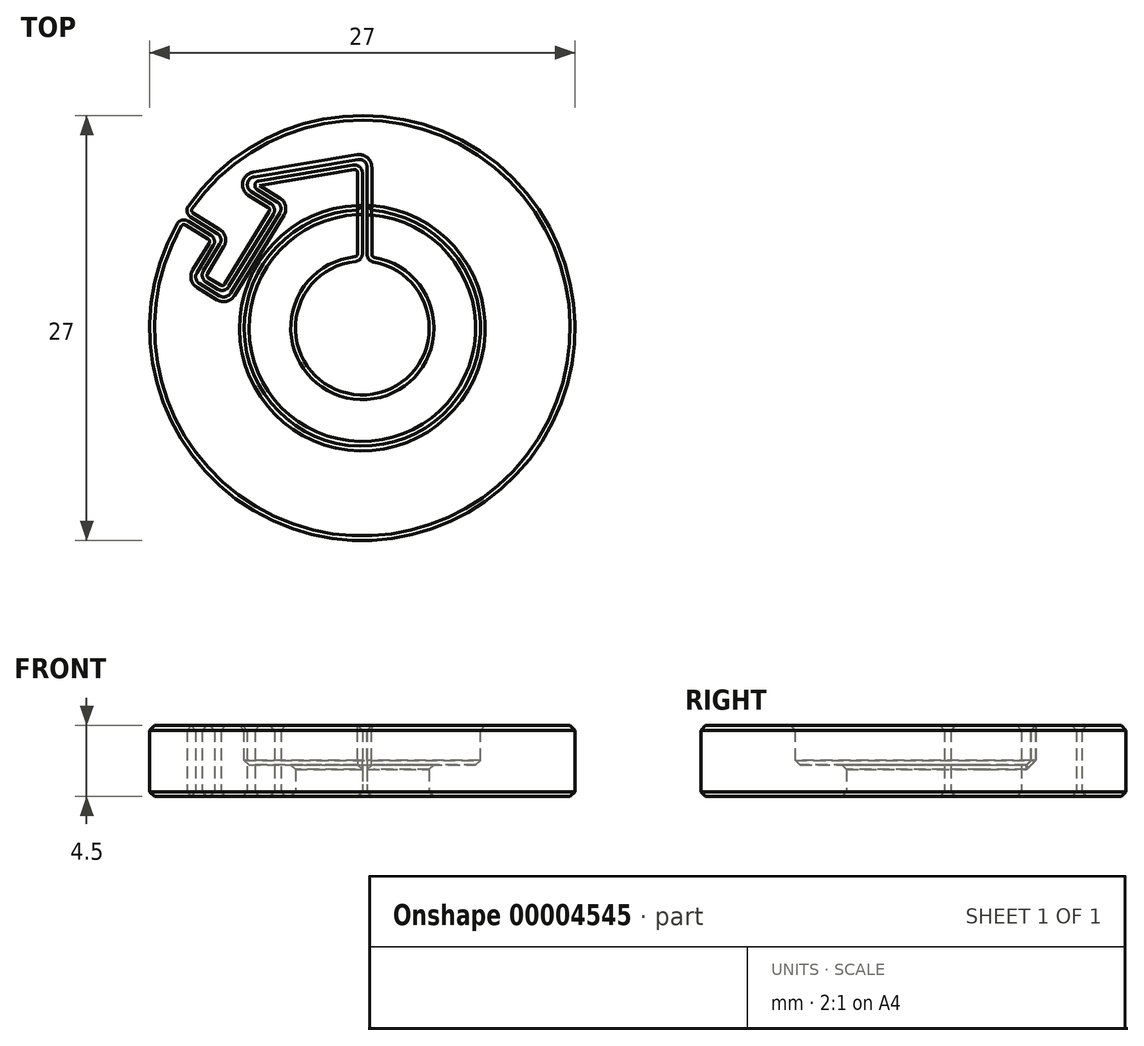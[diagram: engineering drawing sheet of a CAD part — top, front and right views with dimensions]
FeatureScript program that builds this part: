
annotation { "Feature Type Name" : "Feature", "Feature Type Description" : "" }
export const myFeature = defineFeature(function(context is Context, id is Id, definition is map)
    precondition{}
    {
        {
            var Q0;
            Q0=qCreatedBy(makeId("Top.planeOp"),FACE);
            var sketch = newSketch(context, id + "F0", { "sketchPlane" : qUnion([Q0])});
            skArc(sketch, "E0", {"start": v(-0.45, 4.23) * mm, "mid": v(-0.14, -4.25) * mm, "end": v(0.72, 4.19) * mm});
            skArc(sketch, "E1", {"start": v(-11.77, 6.62) * mm, "mid": v(11.42, -7.2) * mm, "end": v(-11.05, 7.76) * mm});
            skLineSegment(sketch, "E2", {"start": v(0, 13.5) * mm, "end": v(0, 4.25) * mm, "construction": true});
            skLineSegment(sketch, "E3", {"start": v(-0.58, 10.35) * mm, "end": v(-6.58, 9.35) * mm});
            skLineSegment(sketch, "E4", {"start": v(-6.69, 8.8) * mm, "end": v(-5.4, 8.01) * mm});
            skLineSegment(sketch, "E5", {"start": v(-9.63, 5.91) * mm, "end": v(-11.07, 6.8) * mm});
            skLineSegment(sketch, "E6", {"start": v(0, 9.86) * mm, "end": v(0, 4.72) * mm});
            skLineSegment(sketch, "E7.0", {"start": v(-9.22, 6.01) * mm, "end": v(-10.9, 7.04) * mm});
            skLineSegment(sketch, "E7.1", {"start": v(0.3, 10.21) * mm, "end": v(0.3, 4.68) * mm});
            skLineSegment(sketch, "E7.2", {"start": v(-0.28, 10.7) * mm, "end": v(-6.9, 9.6) * mm});
            skLineSegment(sketch, "E7.3", {"start": v(-7.07, 8.68) * mm, "end": v(-5.82, 7.91) * mm});
            skPoint(sketch, "E8.visualSharp", {"position": v(0, 10.45) * mm});
            skArc(sketch, "E8.filletArc", {"start": v(0, 9.86) * mm, "mid": v(-0.18, 10.24) * mm, "end": v(-0.58, 10.35) * mm});
            skPoint(sketch, "E9.visualSharp", {"position": v(-7.37, 9.22) * mm});
            skArc(sketch, "E9.filletArc", {"start": v(-6.58, 9.35) * mm, "mid": v(-6.82, 9.11) * mm, "end": v(-6.69, 8.8) * mm});
            skArc(sketch, "E10.filletArc", {"start": v(-5.24, 7.33) * mm, "mid": v(-5.18, 7.7) * mm, "end": v(-5.4, 8.01) * mm});
            skPoint(sketch, "E11.visualSharp", {"position": v(-6.4, 3.92) * mm});
            skPoint(sketch, "E12.visualSharp", {"position": v(-6.45, 4.31) * mm});
            skPoint(sketch, "E13.visualSharp", {"position": v(-4.54, 7.13) * mm});
            skArc(sketch, "E13.filletArc", {"start": v(-5.65, 7.23) * mm, "mid": v(-5.6, 7.6) * mm, "end": v(-5.82, 7.91) * mm});
            skPoint(sketch, "E14.visualSharp", {"position": v(0.3, 10.8) * mm});
            skArc(sketch, "E14.filletArc", {"start": v(0.3, 10.21) * mm, "mid": v(0.12, 10.6) * mm, "end": v(-0.28, 10.7) * mm});
            skPoint(sketch, "E15.visualSharp", {"position": v(-8.2, 9.38) * mm});
            skArc(sketch, "E15.filletArc", {"start": v(-6.9, 9.6) * mm, "mid": v(-7.3, 9.2) * mm, "end": v(-7.07, 8.68) * mm});
            skLineSegment(sketch, "E16", {"start": v(-9.47, 5.22) * mm, "end": v(-10.51, 3.52) * mm});
            skLineSegment(sketch, "E17", {"start": v(-10.35, 2.83) * mm, "end": v(-9.07, 2.05) * mm});
            skLineSegment(sketch, "E18", {"start": v(-8.38, 2.21) * mm, "end": v(-5.24, 7.33) * mm});
            skLineSegment(sketch, "E19.0", {"start": v(-8.48, 2.62) * mm, "end": v(-5.65, 7.23) * mm});
            skLineSegment(sketch, "E19.1", {"start": v(-9.93, 2.93) * mm, "end": v(-9.17, 2.46) * mm});
            skLineSegment(sketch, "E19.2", {"start": v(-9.05, 5.32) * mm, "end": v(-10.1, 3.62) * mm});
            skPoint(sketch, "E20.visualSharp", {"position": v(-8.64, 1.79) * mm});
            skArc(sketch, "E20.filletArc", {"start": v(-9.07, 2.05) * mm, "mid": v(-8.7, 1.99) * mm, "end": v(-8.38, 2.21) * mm});
            skPoint(sketch, "E21.visualSharp", {"position": v(-10.77, 3.1) * mm});
            skArc(sketch, "E21.filletArc", {"start": v(-10.51, 3.52) * mm, "mid": v(-10.57, 3.14) * mm, "end": v(-10.35, 2.83) * mm});
            skPoint(sketch, "E22.visualSharp", {"position": v(-10.36, 3.2) * mm});
            skArc(sketch, "E22.filletArc", {"start": v(-10.1, 3.62) * mm, "mid": v(-10.16, 3.24) * mm, "end": v(-9.93, 2.93) * mm});
            skPoint(sketch, "E23.visualSharp", {"position": v(-8.74, 2.2) * mm});
            skArc(sketch, "E23.filletArc", {"start": v(-9.17, 2.46) * mm, "mid": v(-8.79, 2.4) * mm, "end": v(-8.48, 2.62) * mm});
            skPoint(sketch, "E24.visualSharp", {"position": v(-9.2, 5.65) * mm});
            skArc(sketch, "E24.filletArc", {"start": v(-9.47, 5.22) * mm, "mid": v(-9.4, 5.6) * mm, "end": v(-9.63, 5.91) * mm});
            skPoint(sketch, "E25.visualSharp", {"position": v(-8.8, 5.75) * mm});
            skArc(sketch, "E25.filletArc", {"start": v(-9.05, 5.32) * mm, "mid": v(-9, 5.7) * mm, "end": v(-9.22, 6.01) * mm});
            skPoint(sketch, "E26.visualSharp", {"position": v(-11.5, 7.06) * mm});
            skArc(sketch, "E26.filletArc", {"start": v(-11.07, 6.8) * mm, "mid": v(-11.46, 6.85) * mm, "end": v(-11.77, 6.62) * mm});
            skPoint(sketch, "E27.visualSharp", {"position": v(-11.35, 7.32) * mm});
            skArc(sketch, "E27.filletArc", {"start": v(-11.05, 7.76) * mm, "mid": v(-11.13, 7.37) * mm, "end": v(-10.9, 7.04) * mm});
            skPoint(sketch, "E28.visualSharp", {"position": v(0, 4.25) * mm});
            skArc(sketch, "E28.filletArc", {"start": v(-0.45, 4.23) * mm, "mid": v(-0.13, 4.39) * mm, "end": v(0, 4.72) * mm});
            skPoint(sketch, "E29.visualSharp", {"position": v(0.3, 4.24) * mm});
            skArc(sketch, "E29.filletArc", {"start": v(0.3, 4.68) * mm, "mid": v(0.42, 4.36) * mm, "end": v(0.72, 4.19) * mm});
            skSolve(sketch);
        }
        {
            var Q0;
            Q0=makeQuery(id+"F0.imprint","IMPRINT",FACE,{"disambiguationData":[TD([[makeQuery(id+"F0.imprint","IMPRINT",EDGE,{"derivedFrom":sQuery(id+"F0.wireOp",EDGE,"E3")}),1.0]])]});
            extrude(context, id + "F1", {"entities" : qUnion([Q0]), "depth" : (2 + 2.5) * mm, "offsetDistance" : 25 * mm});
        }
        {
            var Q0;
            Q0=makeQuery(id+"F1.opExtrude","CAP_FACE",FACE,{"disambiguationData":[OSD([sQuery(id+"F0.wireOp",EDGE,"E0"),sQuery(id+"F0.wireOp",EDGE,"E1"),sQuery(id+"F0.wireOp",EDGE,"E3"),sQuery(id+"F0.wireOp",EDGE,"E4"),sQuery(id+"F0.wireOp",EDGE,"27mV3W1z-r9zT-I5jQ-fDVQ-ZefElLG8ptBj"),sQuery(id+"F0.wireOp",EDGE,"E5"),sQuery(id+"F0.wireOp",EDGE,"E6"),sQuery(id+"F0.wireOp",EDGE,"E7.0"),sQuery(id+"F0.wireOp",EDGE,"E7.1"),sQuery(id+"F0.wireOp",EDGE,"E7.2"),sQuery(id+"F0.wireOp",EDGE,"E7.3"),sQuery(id+"F0.wireOp",EDGE,"E7.4")])],"isStart":false});
            var sketch = newSketch(context, id + "F2", { "sketchPlane" : qUnion([Q0])});
            skCircle(sketch, "E30", {"center": v(0, 0) * mm, "radius": 7.5 * mm});
            skSolve(sketch);
        }
        {
            var Q0;
            Q0 = qSketchRegion(id + "F2", true);
            extrude(context, id + "F3", {"entities" : qUnion([Q0]), "operationType" : NewBodyOperationType.REMOVE, "oppositeDirection" : true, "depth" : 2.5 * mm, "offsetDistance" : 25 * mm});
        }
        {
            var Q0;
            Q0=makeQuery(id+"F1.opExtrude","CAP_FACE",FACE,{"disambiguationData":[OSD([sQuery(id+"F0.wireOp",EDGE,"E0"),sQuery(id+"F0.wireOp",EDGE,"E1"),sQuery(id+"F0.wireOp",EDGE,"E3"),sQuery(id+"F0.wireOp",EDGE,"E4"),sQuery(id+"F0.wireOp",EDGE,"E5"),sQuery(id+"F0.wireOp",EDGE,"E6"),sQuery(id+"F0.wireOp",EDGE,"E7.0"),sQuery(id+"F0.wireOp",EDGE,"E7.1"),sQuery(id+"F0.wireOp",EDGE,"E7.2"),sQuery(id+"F0.wireOp",EDGE,"E7.3"),sQuery(id+"F0.wireOp",EDGE,"E8.filletArc"),sQuery(id+"F0.wireOp",EDGE,"E9.filletArc"),sQuery(id+"F0.wireOp",EDGE,"E10.filletArc"),sQuery(id+"F0.wireOp",EDGE,"E13.filletArc"),sQuery(id+"F0.wireOp",EDGE,"E14.filletArc"),sQuery(id+"F0.wireOp",EDGE,"E15.filletArc"),sQuery(id+"F0.wireOp",EDGE,"E16"),sQuery(id+"F0.wireOp",EDGE,"E17"),sQuery(id+"F0.wireOp",EDGE,"E18"),sQuery(id+"F0.wireOp",EDGE,"E19.0"),sQuery(id+"F0.wireOp",EDGE,"E19.1"),sQuery(id+"F0.wireOp",EDGE,"E19.2"),sQuery(id+"F0.wireOp",EDGE,"E20.filletArc"),sQuery(id+"F0.wireOp",EDGE,"E21.filletArc"),sQuery(id+"F0.wireOp",EDGE,"E22.filletArc"),sQuery(id+"F0.wireOp",EDGE,"E23.filletArc"),sQuery(id+"F0.wireOp",EDGE,"E24.filletArc"),sQuery(id+"F0.wireOp",EDGE,"E25.filletArc"),sQuery(id+"F0.wireOp",EDGE,"E26.filletArc"),sQuery(id+"F0.wireOp",EDGE,"E27.filletArc"),sQuery(id+"F0.wireOp",EDGE,"E28.filletArc"),sQuery(id+"F0.wireOp",EDGE,"E29.filletArc")])],"isStart":true});
            var Q1;
            Q1=makeQuery(id+"F1.opExtrude","CAP_FACE",FACE,{"disambiguationData":[OSD([sQuery(id+"F0.wireOp",EDGE,"E0"),sQuery(id+"F0.wireOp",EDGE,"E1"),sQuery(id+"F0.wireOp",EDGE,"E3"),sQuery(id+"F0.wireOp",EDGE,"E4"),sQuery(id+"F0.wireOp",EDGE,"E5"),sQuery(id+"F0.wireOp",EDGE,"E6"),sQuery(id+"F0.wireOp",EDGE,"E7.0"),sQuery(id+"F0.wireOp",EDGE,"E7.1"),sQuery(id+"F0.wireOp",EDGE,"E7.2"),sQuery(id+"F0.wireOp",EDGE,"E7.3"),sQuery(id+"F0.wireOp",EDGE,"E8.filletArc"),sQuery(id+"F0.wireOp",EDGE,"E9.filletArc"),sQuery(id+"F0.wireOp",EDGE,"E10.filletArc"),sQuery(id+"F0.wireOp",EDGE,"E13.filletArc"),sQuery(id+"F0.wireOp",EDGE,"E14.filletArc"),sQuery(id+"F0.wireOp",EDGE,"E15.filletArc"),sQuery(id+"F0.wireOp",EDGE,"E16"),sQuery(id+"F0.wireOp",EDGE,"E17"),sQuery(id+"F0.wireOp",EDGE,"E18"),sQuery(id+"F0.wireOp",EDGE,"E19.0"),sQuery(id+"F0.wireOp",EDGE,"E19.1"),sQuery(id+"F0.wireOp",EDGE,"E19.2"),sQuery(id+"F0.wireOp",EDGE,"E20.filletArc"),sQuery(id+"F0.wireOp",EDGE,"E21.filletArc"),sQuery(id+"F0.wireOp",EDGE,"E22.filletArc"),sQuery(id+"F0.wireOp",EDGE,"E23.filletArc"),sQuery(id+"F0.wireOp",EDGE,"E24.filletArc"),sQuery(id+"F0.wireOp",EDGE,"E25.filletArc"),sQuery(id+"F0.wireOp",EDGE,"E26.filletArc"),sQuery(id+"F0.wireOp",EDGE,"E27.filletArc"),sQuery(id+"F0.wireOp",EDGE,"E28.filletArc"),sQuery(id+"F0.wireOp",EDGE,"E29.filletArc")])],"isStart":false});
            var Q2;
            Q2=makeQuery(id+"F3.boolean.opBoolean","COPY",FACE,{"derivedFrom":makeQuery(id+"F3.opExtrude","CAP_FACE",FACE,{"disambiguationData":[OSD([sQuery(id+"F2.wireOp",EDGE,"E30")])],"isStart":false})});
            chamfer(context, id + "F4", {"entities" : qUnion([Q0, Q1, Q2]), "width" : 0.3 * mm, "tangentPropagation" : true});
        }
    });
